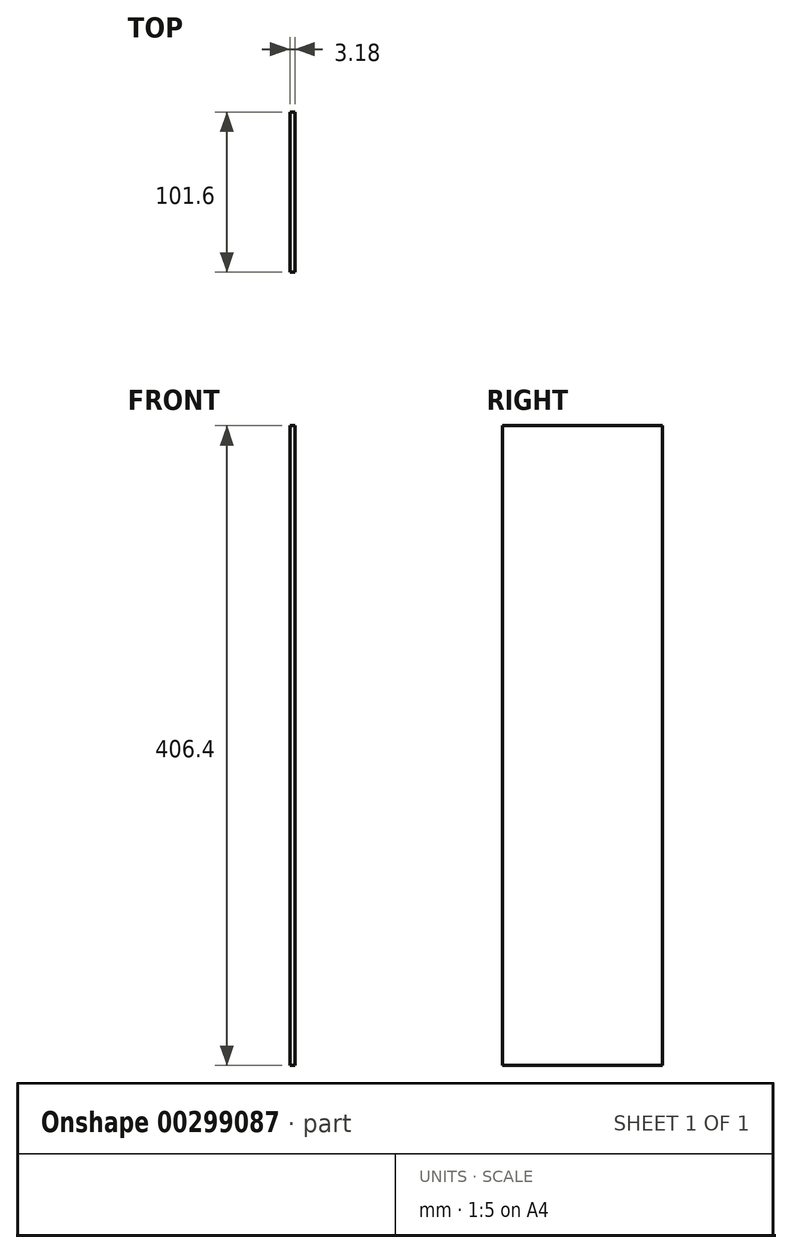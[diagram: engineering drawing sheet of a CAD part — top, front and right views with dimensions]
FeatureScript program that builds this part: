
annotation { "Feature Type Name" : "Feature", "Feature Type Description" : "" }
export const myFeature = defineFeature(function(context is Context, id is Id, definition is map)
    precondition{}
    {
        {
            var Q0;
            Q0=qCreatedBy(makeId("Right.planeOp"),FACE);
            var sketch = newSketch(context, id + "F0", { "sketchPlane" : qUnion([Q0])});
            skLineSegment(sketch, "E0.bottom", {"start": v(-50.8, 203.2) * mm, "end": v(50.8, 203.2) * mm});
            skLineSegment(sketch, "E0.top", {"start": v(-50.8, -203.2) * mm, "end": v(50.8, -203.2) * mm});
            skLineSegment(sketch, "E0.left", {"start": v(-50.8, 203.2) * mm, "end": v(-50.8, -203.2) * mm});
            skLineSegment(sketch, "E0.right", {"start": v(50.8, 203.2) * mm, "end": v(50.8, -203.2) * mm});
            skPoint(sketch, "E0.middle", {"position": v(0, 0) * mm});
            skSolve(sketch);
        }
        {
            var Q0;
            Q0=makeQuery(id+"F0.imprint","IMPRINT",FACE,{"disambiguationData":[TD([[makeQuery(id+"F0.imprint","IMPRINT",EDGE,{"derivedFrom":sQuery(id+"F0.wireOp",EDGE,"E0.bottom")}),-1.0]])]});
            extrude(context, id + "F1", {"entities" : qUnion([Q0]), "endBound" : BoundingType.SYMMETRIC, "depth" : 3.17 * mm});
        }
    });
